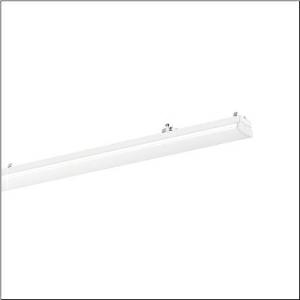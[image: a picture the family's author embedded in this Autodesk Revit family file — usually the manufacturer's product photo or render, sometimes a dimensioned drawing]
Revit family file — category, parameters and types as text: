
# Revit family: licross_r__11_recessed_opal_mo_51te1d7n44xg_9f11
name_source: partatom
category: Lighting Fixtures
units: mm (PartAtom-declared; Revit-internal decimal feet)

## family parameters
Cut with Voids When Loaded = No
Host = Face
Light Source = No
Part Type = Normal
Room Calculation Point = No
Round Connector Dimension = Use Diameter
Shared = No

## types (1)
- Licross® 11 recessed opal MO (1 x LED, 4480 lm, 24.8 W, 4000K)
    Apparent Load = 25 VA
    CIE Flux Codes = 44 73 91 87 100
    Color Rendering = 80
    Color Temperature = 4000K
    Default Elevation = 1800 mm
    Description = Licross® 11 recessed opal MO, luminaire insert, of sheet steel, coil coated, white, length: 1.500mm, width: 76mm, height: 87mm, LED rated luminous flux: 4.480lm, light colour: 840, control gear: ON/OFF, with plug, 3-pole, with phase selection, mains connection: 220..240V, AC, 50/60Hz, rated input power: 25W, internal wiring halogen-free, primary optical cover: cover, of PMMA, light emission: direct with ceiling illumination distribution, primary light characteristic: symmetric, protection rating (complete): IP54, insulation class (complete): insulation class I (protective earthing), certification: CE, ENEC, VDE, UKCA, protection symbol: D if used in an environment with non-conductive dust loads with corresponding accessories, impact resistance: IK06, permissible ambient temperature for indoor applications: -35..+45°C, corresponds to IFS (International Featured Standards) requirements for safety and quality in the food industry, reducing of maximum allowable ambient temperature of 5°C with ceiling mounting, packaging unit: 1 piece
    Height = 83 mm
    Lamp = 1 x LED
    Lamp Light Flux = 4480 lm
    Lamp Power = 24.8 W
    Lamp count = 1
    Length = 1500 mm
    Luminous efficacy = 181 lm/W
    Manufacturer = Siteco
    ModVariant = No
    Model = 51TE1D7N44XG
    Mounting Place = Ceiling
    Mounting Type = Pendant
    Number of Poles = 1
    OnlyDefault = Yes
    Power Factor = 1
    Product Name = Licross® 11 recessed opal MO
    Product group = luminaire insert | ceiling pendant
    ProductGroupID = 902
    Protection Class = Protection class I
    Protection Degree = IP 54
    RLX_Detail_Level = 1
    RLX_Emergency_Light_Flux = 0 lm
    RLX_Emergency_Type = 0
    RLX_Emergency_Type_DB = No
    RlxData = <blob elided: 23133 chars, md5=9d272212>
    Socket = socket
    Standby Power = 0 W
    System Light Flux = 4480 lm
    System Power = 25 W
    Type Comments = Product without accessories
    Type Image = l_1313666.jpg
    URL = http://relux.com
    VarID = ---
    Voltage = 0 V
    Weight = 0.00 kg
    Width = 76 mm

## geometry (parser evidence)
native form markers: Blend x4, Sweep x14
no freeform markers — native parametric forms only
